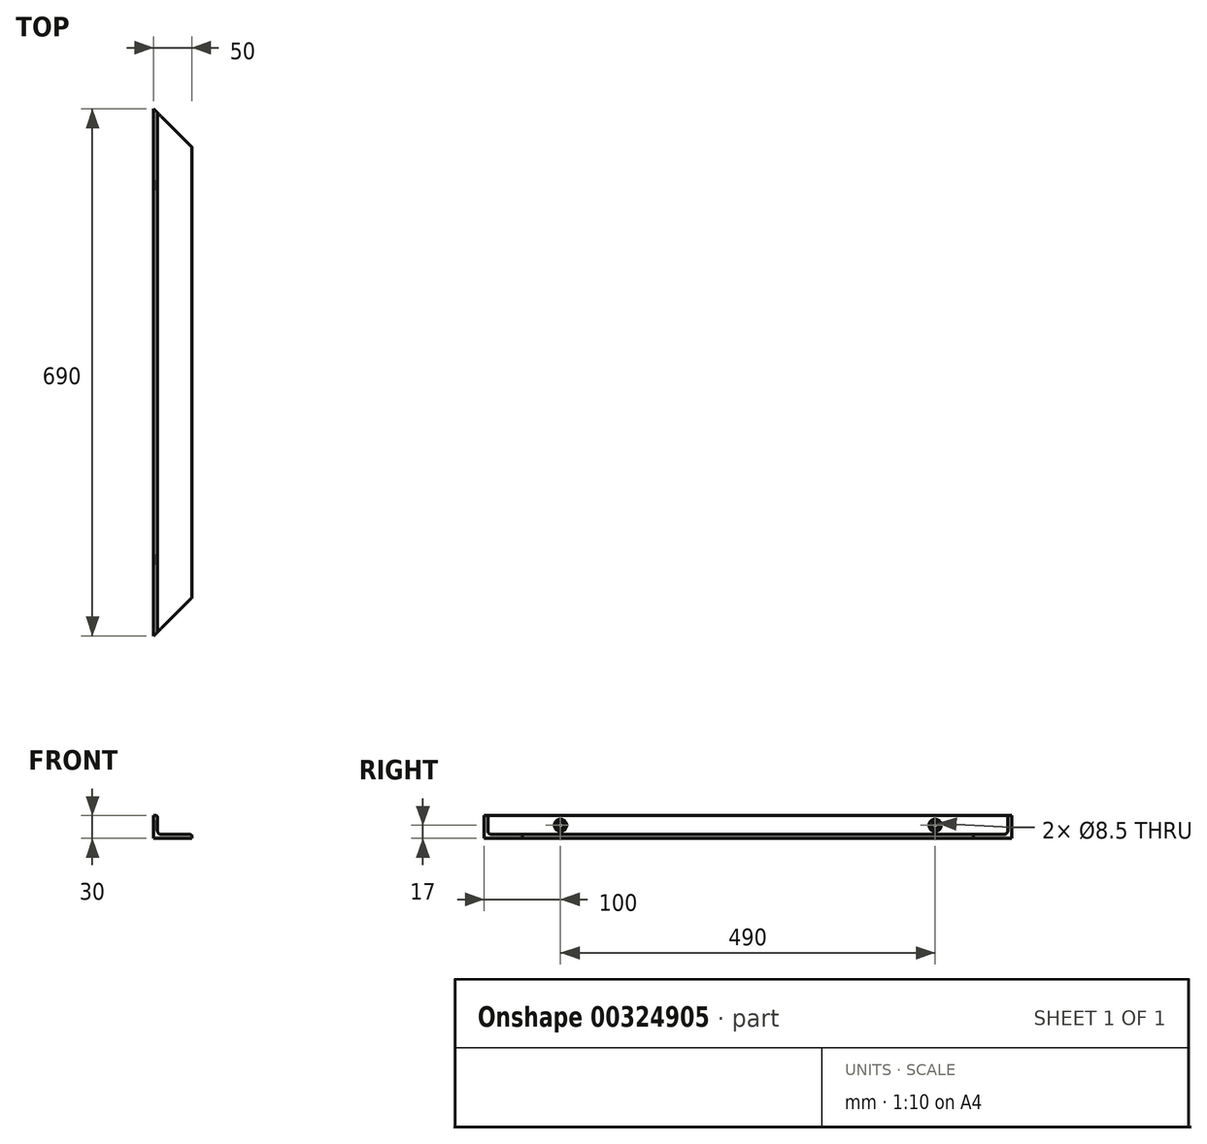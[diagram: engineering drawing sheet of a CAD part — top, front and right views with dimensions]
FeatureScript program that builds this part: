
annotation { "Feature Type Name" : "Feature", "Feature Type Description" : "" }
export const myFeature = defineFeature(function(context is Context, id is Id, definition is map)
    precondition{}
    {
        {
            var Q0;
            Q0=qCreatedBy(makeId("Front.planeOp"),FACE);
            var sketch = newSketch(context, id + "F0", { "sketchPlane" : qUnion([Q0])});
            skLineSegment(sketch, "E0.bottom", {"start": v(0, 0) * mm, "end": v(5, 0) * mm});
            skLineSegment(sketch, "E0.top", {"start": v(0, 30) * mm, "end": v(2.5, 30) * mm});
            skLineSegment(sketch, "E0.left", {"start": v(0, 0) * mm, "end": v(0, 30) * mm});
            skLineSegment(sketch, "E0.right", {"start": v(5, 10) * mm, "end": v(5, 27.5) * mm});
            skLineSegment(sketch, "E1.bottom", {"start": v(0, 0) * mm, "end": v(50, 0) * mm});
            skLineSegment(sketch, "E1.top", {"start": v(10, 5) * mm, "end": v(47.5, 5) * mm});
            skLineSegment(sketch, "E1.left", {"start": v(0, 0) * mm, "end": v(0, 5) * mm});
            skLineSegment(sketch, "E1.right", {"start": v(50, 0) * mm, "end": v(50, 2.5) * mm});
            skPoint(sketch, "E2.visualSharp", {"position": v(5, 30) * mm});
            skArc(sketch, "E2.filletArc", {"start": v(5, 27.5) * mm, "mid": v(4.27, 29.27) * mm, "end": v(2.5, 30) * mm});
            skPoint(sketch, "E3.visualSharp", {"position": v(50, 5) * mm});
            skArc(sketch, "E3.filletArc", {"start": v(50, 2.5) * mm, "mid": v(49.27, 4.27) * mm, "end": v(47.5, 5) * mm});
            skPoint(sketch, "E4.visualSharp", {"position": v(5, 5) * mm});
            skArc(sketch, "E4.filletArc", {"start": v(5, 10) * mm, "mid": v(6.46, 6.46) * mm, "end": v(10, 5) * mm});
            skSolve(sketch);
        }
        {
            var Q0;
            Q0=makeQuery(id+"F0.imprint","IMPRINT",FACE,{"disambiguationData":[TD([[makeQuery(id+"F0.imprint","IMPRINT",EDGE,{"derivedFrom":sQuery(id+"F0.wireOp",EDGE,"E0.top")}),-1.0]])]});
            extrude(context, id + "F1", {"entities" : qUnion([Q0]), "oppositeDirection" : true, "depth" : 690 * mm});
        }
        {
            var Q0;
            Q0=makeQuery(id+"F1.opExtrude","SWEPT_FACE",FACE,{"disambiguationData":[OSD([sQuery(id+"F0.wireOp",EDGE,"E0.top")])]});
            var sketch = newSketch(context, id + "F2", { "sketchPlane" : qUnion([Q0])});
            skLineSegment(sketch, "E5", {"start": v(-62.59, 345) * mm, "end": v(124.15, 345) * mm, "construction": true});
            skLineSegment(sketch, "E6", {"start": v(0, 0) * mm, "end": v(56.9, 0) * mm});
            skLineSegment(sketch, "E7", {"start": v(56.9, 0) * mm, "end": v(56.9, 56.9) * mm});
            skLineSegment(sketch, "E8", {"start": v(56.9, 56.9) * mm, "end": v(0, 0) * mm});
            skLineSegment(sketch, "E9.MirrorCS", {"start": v(56.9, 633.1) * mm, "end": v(0, 690) * mm});
            skLineSegment(sketch, "E10.MirrorCS", {"start": v(56.9, 690) * mm, "end": v(56.9, 633.1) * mm});
            skLineSegment(sketch, "E11.MirrorCS", {"start": v(0, 690) * mm, "end": v(56.9, 690) * mm});
            skSolve(sketch);
        }
        {
            var Q0;
            {var subQ3=sQuery(id+"F2.wireOp",EDGE,"E7");Q0=makeQuery(id+"F2.imprint","IMPRINT",FACE,{"disambiguationData":[TD([[makeQuery(id+"F2.imprint","IMPRINT",EDGE,{"derivedFrom":subQ3}),1.0]])]});}
            var Q1;
            {var subQ0=sQuery(id+"F2.wireOp",EDGE,"E10.MirrorCS");Q1=makeQuery(id+"F2.imprint","IMPRINT",FACE,{"disambiguationData":[TD([[makeQuery(id+"F2.imprint","IMPRINT",EDGE,{"derivedFrom":subQ0}),-1.0]])]});}
            var Q2;
            {var subQ1=sQuery(id+"F2.wireOp",EDGE,"E9.MirrorCS");var subQ2=sQuery(id+"F0.wireOp",EDGE,"E0.top");var subQ4=makeQuery(id+"F1.opExtrude","SWEPT_EDGE",EDGE,{"disambiguationData":[OSD([subQ2,sQuery(id+"F0.wireOp",EDGE,"E2.filletArc")])]});var subQ5=makeQuery(id+"F2.imprint","INTERSECT",VERTEX,{"derivedFrom":[subQ4,subQ1]});Q2=makeQuery(id+"F2.imprint","IMPRINT",FACE,{"disambiguationData":[TD([[makeQuery(id+"F2.imprint","IMPRINT",EDGE,{"disambiguationData":[TD([[subQ5,-1.0]])],"derivedFrom":subQ1}),-1.0]])]});}
            var Q3;
            {var subQ1=sQuery(id+"F2.wireOp",EDGE,"E6");var subQ2=sQuery(id+"F0.wireOp",EDGE,"E0.top");var subQ4=makeQuery(id+"F1.opExtrude","SWEPT_EDGE",EDGE,{"disambiguationData":[OSD([subQ2,sQuery(id+"F0.wireOp",EDGE,"E2.filletArc")])]});var subQ5=makeQuery(id+"F2.imprint","INTERSECT",VERTEX,{"derivedFrom":[subQ4,subQ1]});Q3=makeQuery(id+"F2.imprint","IMPRINT",FACE,{"disambiguationData":[TD([[makeQuery(id+"F2.imprint","IMPRINT",EDGE,{"disambiguationData":[TD([[subQ5,1.0]])],"derivedFrom":subQ1}),1.0]])]});}
            extrude(context, id + "F3", {"entities" : qUnion([Q0, Q1, Q2, Q3]), "operationType" : NewBodyOperationType.REMOVE, "endBound" : BoundingType.THROUGH_ALL, "oppositeDirection" : true, "depth" : 25 * mm});
        }
        {
            var Q0;
            Q0=makeQuery(id+"F1.opExtrude","SWEPT_FACE",FACE,{"disambiguationData":[OSD([sQuery(id+"F0.wireOp",EDGE,"E0.left"),sQuery(id+"F0.wireOp",EDGE,"E1.left")])]});
            var sketch = newSketch(context, id + "F4", { "sketchPlane" : qUnion([Q0])});
            skLineSegment(sketch, "E12", {"start": v(488.91, 17) * mm, "end": v(-1217.03, 17) * mm, "construction": true});
            skLineSegment(sketch, "E13", {"start": v(-345, -8.53) * mm, "end": v(-345, 58.74) * mm, "construction": true});
            skCircle(sketch, "E14", {"center": v(-100, 17) * mm, "radius": 4.25 * mm});
            skCircle(sketch, "E15", {"center": v(-590, 17) * mm, "radius": 4.25 * mm});
            skSolve(sketch);
        }
        {
            var Q0;
            Q0=makeQuery(id+"F4.imprint","IMPRINT",FACE,{"disambiguationData":[TD([[makeQuery(id+"F4.imprint","IMPRINT",EDGE,{"derivedFrom":sQuery(id+"F4.wireOp",EDGE,"E14")}),1.0]])]});
            var Q1;
            Q1=makeQuery(id+"F4.imprint","IMPRINT",FACE,{"disambiguationData":[TD([[makeQuery(id+"F4.imprint","IMPRINT",EDGE,{"derivedFrom":sQuery(id+"F4.wireOp",EDGE,"E15")}),1.0]])]});
            extrude(context, id + "F5", {"entities" : qUnion([Q0, Q1]), "operationType" : NewBodyOperationType.REMOVE, "endBound" : BoundingType.THROUGH_ALL, "oppositeDirection" : true, "depth" : 25 * mm});
        }
        {
            var Q0;
            Q0=makeQuery(id+"F5.boolean.opBoolean","INTERSECT",EDGE,{"derivedFrom":[makeQuery(id+"F1.opExtrude","SWEPT_FACE",FACE,{"disambiguationData":[OSD([sQuery(id+"F0.wireOp",EDGE,"E0.right")])]}),makeQuery(id+"F5.opExtrude","SWEPT_FACE",FACE,{"disambiguationData":[OSD([sQuery(id+"F4.wireOp",EDGE,"E14")])]})]});
            var Q1;
            Q1=makeQuery(id+"F5.boolean.opBoolean","INTERSECT",EDGE,{"derivedFrom":[makeQuery(id+"F1.opExtrude","SWEPT_FACE",FACE,{"disambiguationData":[OSD([sQuery(id+"F0.wireOp",EDGE,"E0.right")])]}),makeQuery(id+"F5.opExtrude","SWEPT_FACE",FACE,{"disambiguationData":[OSD([sQuery(id+"F4.wireOp",EDGE,"E15")])]})]});
            chamfer(context, id + "F6", {"entities" : qUnion([Q0, Q1]), "width" : 3.7 * mm, "tangentPropagation" : true});
        }
    });
